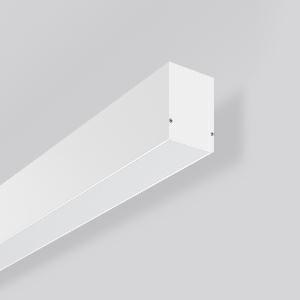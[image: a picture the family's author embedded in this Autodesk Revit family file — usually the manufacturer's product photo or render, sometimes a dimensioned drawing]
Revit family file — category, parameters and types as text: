
# Revit family: less_is_more_50_312611_002_1_76_c31a
name_source: partatom
category: Lighting Fixtures
units: mm (PartAtom-declared; Revit-internal decimal feet)

## family parameters
Cut with Voids When Loaded = No
Host = Face
Light Source = No
Part Type = Normal
Room Calculation Point = No
Round Connector Dimension = Use Diameter
Shared = No

## types (1)
- LESS IS MORE 50 (1 x LED Modul 840, 2300 lm, 4000)
    Apparent Load = 18 VA
    CIE Flux Codes = 48 80 96 100 100
    Color Rendering = 80
    Color Temperature = 4000
    Default Elevation = 1800 mm
    Description = Series: LESS IS MORE 50
Linear wall luminaires. Housing: extruded aluminium profile, powder-coated. End cap aluminium powder-coated. Diffuser made of non-yellowing plastic (PMMA), opal. Direct light emission. Suitable for Wall (surface). LED unit with integrated converter interchangeable and removable. Suitable for through-wiring. With sensors or as a safety luminaire on request. 
Colour: traffic white, matt (RAL 9016)
Length: 1687 mm
Width: 67 mm
Height: 75 mm
Lamp: LED
Socket: without socket
Colour temperature: 4000K
Colour rendering index (CRI): 80
System power: 18 W
Rated luminous flux: 2300 lm
Luminous efficiency: 128 lm/W
Control gear: Converter, dimmable, DALI
Protection class: I
Type of protection: IP 20
    Height = 75 mm
    Lamp = 1 x LED Modul 840
    Lamp Light Flux = 2300 lm
    Lamp count = 1
    Length = 1687 mm
    Lifetime = 50000 h
    Luminous efficacy = 128 lm/W
    Manufacturer = RZB
    ModVariant = No
    Model = 312611.002.1.76
    Mounting Place = Wall
    Mounting Type = Surface mounted
    Number of Poles = 1
    OnlyDefault = Yes
    Power Factor = 1
    Product Name = LESS IS MORE 50
    Product group = Surface mounted LED linear luminaires
    ProductGroupID = 2007
    Protection Class = Protection class I
    Protection Degree = IP 20
    RLX_Detail_Level = 1
    RLX_Emergency_Light_Flux = 0 lm
    RLX_Emergency_Type = 0
    RLX_Emergency_Type_DB = No
    RlxData = <blob elided: 35181 chars, md5=d1835e33>
    Socket = socket
    Standby Power = 0 W
    System Light Flux = 2300 lm
    System Power = 18 W
    Type Comments = Product without accessories
    Type Image = 312606.002.jpg
    URL = http://relux.com
    VarID = ---
    Voltage = 0 V
    Weight = 0.00 kg
    Width = 67 mm

## geometry (parser evidence)
native form markers: Blend x4, Sweep x10
no freeform markers — native parametric forms only
